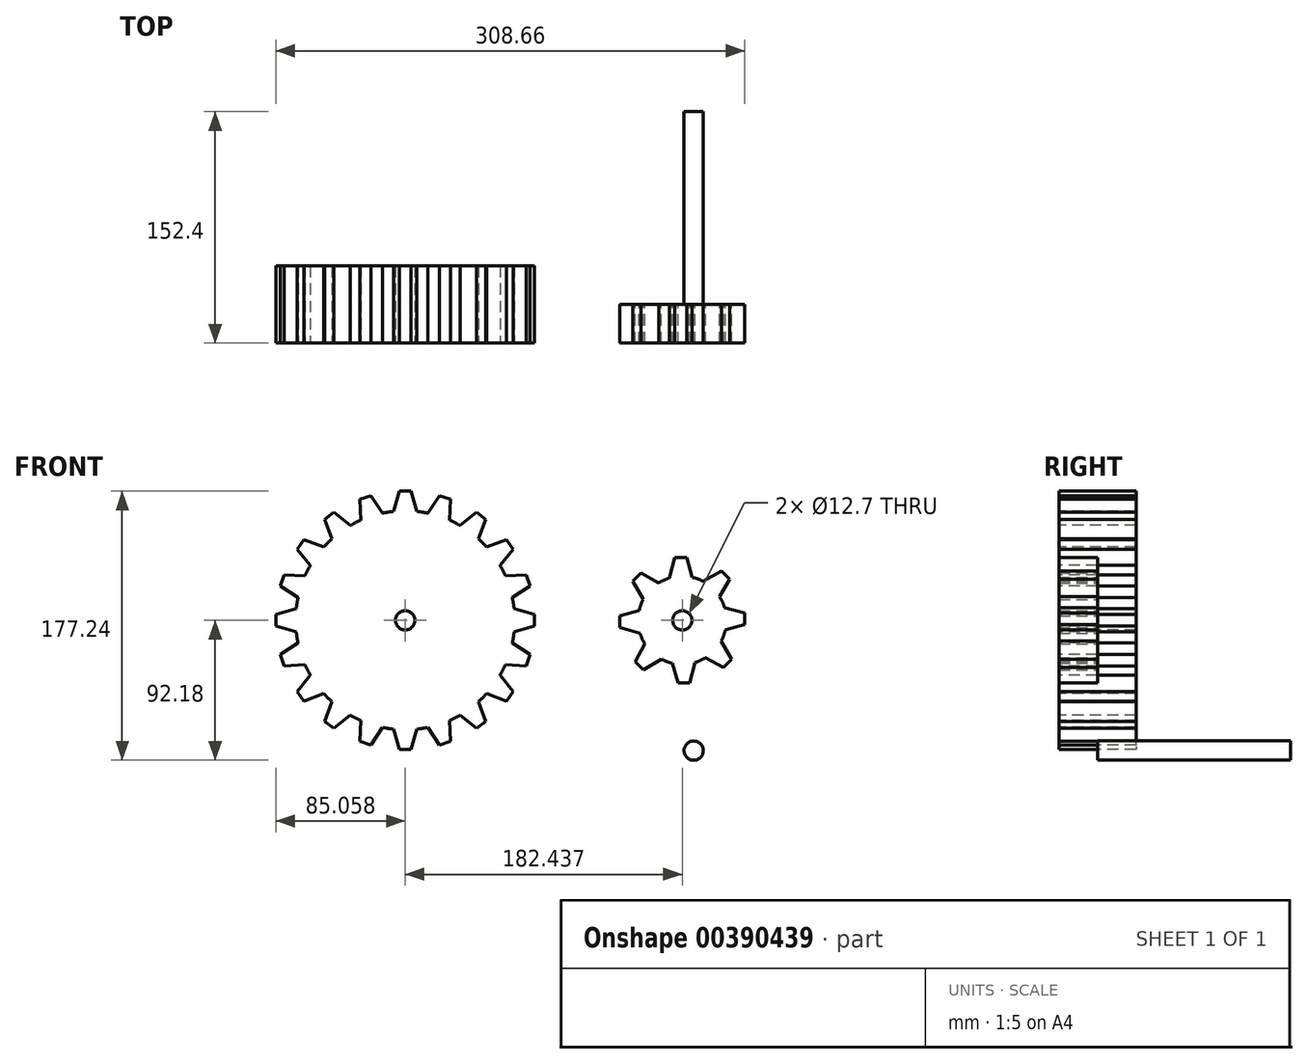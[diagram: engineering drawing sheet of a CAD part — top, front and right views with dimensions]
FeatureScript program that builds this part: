
annotation { "Feature Type Name" : "Feature", "Feature Type Description" : "" }
export const myFeature = defineFeature(function(context is Context, id is Id, definition is map)
    precondition{}
    {
        {
            var Q0;
            Q0=qCreatedBy(makeId("Front.planeOp"),FACE);
            var sketch = newSketch(context, id + "F0", { "sketchPlane" : qUnion([Q0])});
            skCircle(sketch, "E0", {"center": v(-135.26, 0) * mm, "radius": 72.11 * mm});
            skCircle(sketch, "E1", {"center": v(47.17, 0) * mm, "radius": 29.08 * mm});
            skLineSegment(sketch, "E2", {"start": v(-63.54, -7.5) * mm, "end": v(-50.2, -3.89) * mm});
            skLineSegment(sketch, "E3", {"start": v(0, 0) * mm, "end": v(-108.7, 0) * mm, "construction": true});
            skLineSegment(sketch, "E4.MirrorCS", {"start": v(-63.54, 7.5) * mm, "end": v(-50.2, 3.89) * mm});
            skLineSegment(sketch, "E5", {"start": v(-50.2, 3.89) * mm, "end": v(-50.2, -3.89) * mm});
            skLineSegment(sketch, "E6.1.0", {"start": v(-64.73, 15.02) * mm, "end": v(-53.16, 22.59) * mm});
            skLineSegment(sketch, "E6.1.1", {"start": v(-55.57, 29.98) * mm, "end": v(-53.16, 22.59) * mm});
            skLineSegment(sketch, "E6.1.2", {"start": v(-69.37, 29.3) * mm, "end": v(-55.57, 29.98) * mm});
            skLineSegment(sketch, "E6.2.0", {"start": v(-72.83, 36.08) * mm, "end": v(-64.16, 46.85) * mm});
            skLineSegment(sketch, "E6.2.1", {"start": v(-68.73, 53.14) * mm, "end": v(-64.16, 46.85) * mm});
            skLineSegment(sketch, "E6.2.2", {"start": v(-81.65, 48.23) * mm, "end": v(-68.73, 53.14) * mm});
            skLineSegment(sketch, "E6.3.0", {"start": v(-87.03, 53.61) * mm, "end": v(-82.12, 66.53) * mm});
            skLineSegment(sketch, "E6.3.1", {"start": v(-88.4, 71.1) * mm, "end": v(-82.12, 66.53) * mm});
            skLineSegment(sketch, "E6.3.2", {"start": v(-99.18, 62.44) * mm, "end": v(-88.4, 71.1) * mm});
            skLineSegment(sketch, "E6.4.0", {"start": v(-105.96, 65.9) * mm, "end": v(-105.28, 79.7) * mm});
            skLineSegment(sketch, "E6.4.1", {"start": v(-112.67, 82.1) * mm, "end": v(-105.28, 79.7) * mm});
            skLineSegment(sketch, "E6.4.2", {"start": v(-120.24, 70.53) * mm, "end": v(-112.67, 82.1) * mm});
            skLineSegment(sketch, "E6.5.0", {"start": v(-127.76, 71.72) * mm, "end": v(-131.38, 85.06) * mm});
            skLineSegment(sketch, "E6.5.1", {"start": v(-139.15, 85.06) * mm, "end": v(-131.38, 85.06) * mm});
            skLineSegment(sketch, "E6.5.2", {"start": v(-142.77, 71.72) * mm, "end": v(-139.15, 85.06) * mm});
            skLineSegment(sketch, "E6.6.0", {"start": v(-150.29, 70.53) * mm, "end": v(-157.85, 82.1) * mm});
            skLineSegment(sketch, "E6.6.1", {"start": v(-165.24, 79.7) * mm, "end": v(-157.85, 82.1) * mm});
            skLineSegment(sketch, "E6.6.2", {"start": v(-164.56, 65.9) * mm, "end": v(-165.24, 79.7) * mm});
            skLineSegment(sketch, "E6.7.0", {"start": v(-171.35, 62.44) * mm, "end": v(-182.12, 71.1) * mm});
            skLineSegment(sketch, "E6.7.1", {"start": v(-188.4, 66.53) * mm, "end": v(-182.12, 71.1) * mm});
            skLineSegment(sketch, "E6.7.2", {"start": v(-183.5, 53.61) * mm, "end": v(-188.4, 66.53) * mm});
            skLineSegment(sketch, "E6.8.0", {"start": v(-188.87, 48.23) * mm, "end": v(-201.8, 53.14) * mm});
            skLineSegment(sketch, "E6.8.1", {"start": v(-206.36, 46.85) * mm, "end": v(-201.8, 53.14) * mm});
            skLineSegment(sketch, "E6.8.2", {"start": v(-197.7, 36.08) * mm, "end": v(-206.36, 46.85) * mm});
            skLineSegment(sketch, "E6.9.0", {"start": v(-201.15, 29.3) * mm, "end": v(-214.96, 29.98) * mm});
            skLineSegment(sketch, "E6.9.1", {"start": v(-217.36, 22.59) * mm, "end": v(-214.96, 29.98) * mm});
            skLineSegment(sketch, "E6.9.2", {"start": v(-205.8, 15.02) * mm, "end": v(-217.36, 22.59) * mm});
            skLineSegment(sketch, "E6.10.0", {"start": v(-206.98, 7.5) * mm, "end": v(-220.32, 3.89) * mm});
            skLineSegment(sketch, "E6.10.1", {"start": v(-220.32, -3.89) * mm, "end": v(-220.32, 3.89) * mm});
            skLineSegment(sketch, "E6.10.2", {"start": v(-206.98, -7.5) * mm, "end": v(-220.32, -3.89) * mm});
            skLineSegment(sketch, "E6.11.0", {"start": v(-205.8, -15.02) * mm, "end": v(-217.36, -22.59) * mm});
            skLineSegment(sketch, "E6.11.1", {"start": v(-214.96, -29.98) * mm, "end": v(-217.36, -22.59) * mm});
            skLineSegment(sketch, "E6.11.2", {"start": v(-201.15, -29.3) * mm, "end": v(-214.96, -29.98) * mm});
            skLineSegment(sketch, "E6.12.0", {"start": v(-197.7, -36.08) * mm, "end": v(-206.36, -46.85) * mm});
            skLineSegment(sketch, "E6.12.1", {"start": v(-201.8, -53.14) * mm, "end": v(-206.36, -46.85) * mm});
            skLineSegment(sketch, "E6.12.2", {"start": v(-188.87, -48.23) * mm, "end": v(-201.8, -53.14) * mm});
            skLineSegment(sketch, "E6.13.0", {"start": v(-183.5, -53.61) * mm, "end": v(-188.4, -66.53) * mm});
            skLineSegment(sketch, "E6.13.1", {"start": v(-182.12, -71.1) * mm, "end": v(-188.4, -66.53) * mm});
            skLineSegment(sketch, "E6.13.2", {"start": v(-171.35, -62.44) * mm, "end": v(-182.12, -71.1) * mm});
            skLineSegment(sketch, "E6.14.0", {"start": v(-164.56, -65.9) * mm, "end": v(-165.24, -79.7) * mm});
            skLineSegment(sketch, "E6.14.1", {"start": v(-157.85, -82.1) * mm, "end": v(-165.24, -79.7) * mm});
            skLineSegment(sketch, "E6.14.2", {"start": v(-150.29, -70.53) * mm, "end": v(-157.85, -82.1) * mm});
            skLineSegment(sketch, "E6.15.0", {"start": v(-142.77, -71.72) * mm, "end": v(-139.15, -85.06) * mm});
            skLineSegment(sketch, "E6.15.1", {"start": v(-131.38, -85.06) * mm, "end": v(-139.15, -85.06) * mm});
            skLineSegment(sketch, "E6.15.2", {"start": v(-127.76, -71.72) * mm, "end": v(-131.38, -85.06) * mm});
            skLineSegment(sketch, "E6.16.0", {"start": v(-120.24, -70.53) * mm, "end": v(-112.67, -82.1) * mm});
            skLineSegment(sketch, "E6.16.1", {"start": v(-105.28, -79.7) * mm, "end": v(-112.67, -82.1) * mm});
            skLineSegment(sketch, "E6.16.2", {"start": v(-105.96, -65.9) * mm, "end": v(-105.28, -79.7) * mm});
            skLineSegment(sketch, "E6.17.0", {"start": v(-99.18, -62.44) * mm, "end": v(-88.4, -71.1) * mm});
            skLineSegment(sketch, "E6.17.1", {"start": v(-82.12, -66.53) * mm, "end": v(-88.4, -71.1) * mm});
            skLineSegment(sketch, "E6.17.2", {"start": v(-87.03, -53.61) * mm, "end": v(-82.12, -66.53) * mm});
            skLineSegment(sketch, "E6.18.0", {"start": v(-81.65, -48.23) * mm, "end": v(-68.73, -53.14) * mm});
            skLineSegment(sketch, "E6.18.1", {"start": v(-64.16, -46.85) * mm, "end": v(-68.73, -53.14) * mm});
            skLineSegment(sketch, "E6.18.2", {"start": v(-72.83, -36.08) * mm, "end": v(-64.16, -46.85) * mm});
            skLineSegment(sketch, "E6.19.0", {"start": v(-69.37, -29.3) * mm, "end": v(-55.57, -29.98) * mm});
            skLineSegment(sketch, "E6.19.1", {"start": v(-53.16, -22.59) * mm, "end": v(-55.57, -29.98) * mm});
            skLineSegment(sketch, "E6.19.2", {"start": v(-64.73, -15.02) * mm, "end": v(-53.16, -22.59) * mm});
            skLineSegment(sketch, "E7", {"start": v(75.53, -6.43) * mm, "end": v(88.34, -2.82) * mm});
            skLineSegment(sketch, "E8.MirrorCS", {"start": v(75, 8.43) * mm, "end": v(88.34, 4.8) * mm});
            skLineSegment(sketch, "E9", {"start": v(88.34, 4.8) * mm, "end": v(88.34, -2.82) * mm});
            skLineSegment(sketch, "E10.1.0", {"start": v(60.9, 25.64) * mm, "end": v(72.89, 32.5) * mm});
            skLineSegment(sketch, "E10.1.1", {"start": v(72.89, 32.5) * mm, "end": v(78.28, 27.11) * mm});
            skLineSegment(sketch, "E10.1.2", {"start": v(71.77, 15.5) * mm, "end": v(78.28, 27.11) * mm});
            skLineSegment(sketch, "E10.2.0", {"start": v(38.75, 27.83) * mm, "end": v(42.37, 41.17) * mm});
            skLineSegment(sketch, "E10.2.1", {"start": v(42.37, 41.17) * mm, "end": v(50, 41.17) * mm});
            skLineSegment(sketch, "E10.2.2", {"start": v(53.6, 28.36) * mm, "end": v(50, 41.17) * mm});
            skLineSegment(sketch, "E10.3.0", {"start": v(21.54, 13.72) * mm, "end": v(14.67, 25.71) * mm});
            skLineSegment(sketch, "E10.3.1", {"start": v(14.67, 25.71) * mm, "end": v(20.06, 31.1) * mm});
            skLineSegment(sketch, "E10.3.2", {"start": v(31.67, 24.6) * mm, "end": v(20.06, 31.1) * mm});
            skLineSegment(sketch, "E10.4.0", {"start": v(19.35, -8.43) * mm, "end": v(6, -4.8) * mm});
            skLineSegment(sketch, "E10.4.1", {"start": v(6, -4.8) * mm, "end": v(6, 2.82) * mm});
            skLineSegment(sketch, "E10.4.2", {"start": v(18.82, 6.43) * mm, "end": v(6, 2.82) * mm});
            skLineSegment(sketch, "E10.5.0", {"start": v(33.46, -25.64) * mm, "end": v(21.46, -32.5) * mm});
            skLineSegment(sketch, "E10.5.1", {"start": v(21.46, -32.5) * mm, "end": v(16.07, -27.11) * mm});
            skLineSegment(sketch, "E10.5.2", {"start": v(22.58, -15.5) * mm, "end": v(16.07, -27.11) * mm});
            skLineSegment(sketch, "E10.6.0", {"start": v(55.6, -27.83) * mm, "end": v(51.98, -41.17) * mm});
            skLineSegment(sketch, "E10.6.1", {"start": v(51.98, -41.17) * mm, "end": v(44.35, -41.17) * mm});
            skLineSegment(sketch, "E10.6.2", {"start": v(40.75, -28.36) * mm, "end": v(44.35, -41.17) * mm});
            skLineSegment(sketch, "E10.7.0", {"start": v(72.81, -13.72) * mm, "end": v(79.68, -25.71) * mm});
            skLineSegment(sketch, "E10.7.1", {"start": v(79.68, -25.71) * mm, "end": v(74.29, -31.1) * mm});
            skLineSegment(sketch, "E10.7.2", {"start": v(62.68, -24.6) * mm, "end": v(74.29, -31.1) * mm});
            skCircle(sketch, "E11", {"center": v(-135.26, 0) * mm, "radius": 6.35 * mm});
            skCircle(sketch, "E12", {"center": v(47.17, 0) * mm, "radius": 6.35 * mm});
            skCircle(sketch, "E13", {"center": v(36.26, -79.8) * mm, "radius": 6.35 * mm});
            skSolve(sketch);
        }
        {
            var Q0;
            {var subQ0=sQuery(id+"F0.wireOp",EDGE,"E6.9.0");Q0=makeQuery(id+"F0.imprint","IMPRINT",FACE,{"disambiguationData":[TD([[makeQuery(id+"F0.imprint","IMPRINT",EDGE,{"derivedFrom":subQ0}),1.0]])]});}
            var Q1;
            {var subQ0=sQuery(id+"F0.wireOp",EDGE,"E0");var subQ18=makeQuery(id+"F0.imprint","INTERSECT",VERTEX,{"derivedFrom":[subQ0,sQuery(id+"F0.wireOp",EDGE,"E4.MirrorCS")]});Q1=makeQuery(id+"F0.imprint","IMPRINT",FACE,{"disambiguationData":[TD([[makeQuery(id+"F0.imprint","IMPRINT",EDGE,{"disambiguationData":[TD([[subQ18,-1.0]])],"derivedFrom":subQ0}),1.0]])]});}
            var Q2;
            {var subQ0=sQuery(id+"F0.wireOp",EDGE,"E6.8.0");Q2=makeQuery(id+"F0.imprint","IMPRINT",FACE,{"disambiguationData":[TD([[makeQuery(id+"F0.imprint","IMPRINT",EDGE,{"derivedFrom":subQ0}),1.0]])]});}
            var Q3;
            {var subQ0=sQuery(id+"F0.wireOp",EDGE,"E6.7.0");Q3=makeQuery(id+"F0.imprint","IMPRINT",FACE,{"disambiguationData":[TD([[makeQuery(id+"F0.imprint","IMPRINT",EDGE,{"derivedFrom":subQ0}),1.0]])]});}
            var Q4;
            {var subQ0=sQuery(id+"F0.wireOp",EDGE,"E6.6.0");Q4=makeQuery(id+"F0.imprint","IMPRINT",FACE,{"disambiguationData":[TD([[makeQuery(id+"F0.imprint","IMPRINT",EDGE,{"derivedFrom":subQ0}),1.0]])]});}
            var Q5;
            {var subQ0=sQuery(id+"F0.wireOp",EDGE,"E6.5.0");Q5=makeQuery(id+"F0.imprint","IMPRINT",FACE,{"disambiguationData":[TD([[makeQuery(id+"F0.imprint","IMPRINT",EDGE,{"derivedFrom":subQ0}),1.0]])]});}
            var Q6;
            {var subQ0=sQuery(id+"F0.wireOp",EDGE,"E6.4.0");Q6=makeQuery(id+"F0.imprint","IMPRINT",FACE,{"disambiguationData":[TD([[makeQuery(id+"F0.imprint","IMPRINT",EDGE,{"derivedFrom":subQ0}),1.0]])]});}
            var Q7;
            {var subQ0=sQuery(id+"F0.wireOp",EDGE,"E6.3.0");Q7=makeQuery(id+"F0.imprint","IMPRINT",FACE,{"disambiguationData":[TD([[makeQuery(id+"F0.imprint","IMPRINT",EDGE,{"derivedFrom":subQ0}),1.0]])]});}
            var Q8;
            {var subQ0=sQuery(id+"F0.wireOp",EDGE,"E6.2.0");Q8=makeQuery(id+"F0.imprint","IMPRINT",FACE,{"disambiguationData":[TD([[makeQuery(id+"F0.imprint","IMPRINT",EDGE,{"derivedFrom":subQ0}),1.0]])]});}
            var Q9;
            {var subQ0=sQuery(id+"F0.wireOp",EDGE,"E6.1.0");Q9=makeQuery(id+"F0.imprint","IMPRINT",FACE,{"disambiguationData":[TD([[makeQuery(id+"F0.imprint","IMPRINT",EDGE,{"derivedFrom":subQ0}),1.0]])]});}
            var Q10;
            {var subQ0=sQuery(id+"F0.wireOp",EDGE,"E2");Q10=makeQuery(id+"F0.imprint","IMPRINT",FACE,{"disambiguationData":[TD([[makeQuery(id+"F0.imprint","IMPRINT",EDGE,{"derivedFrom":subQ0}),1.0]])]});}
            var Q11;
            {var subQ0=sQuery(id+"F0.wireOp",EDGE,"E6.19.0");Q11=makeQuery(id+"F0.imprint","IMPRINT",FACE,{"disambiguationData":[TD([[makeQuery(id+"F0.imprint","IMPRINT",EDGE,{"derivedFrom":subQ0}),1.0]])]});}
            var Q12;
            {var subQ0=sQuery(id+"F0.wireOp",EDGE,"E6.18.0");Q12=makeQuery(id+"F0.imprint","IMPRINT",FACE,{"disambiguationData":[TD([[makeQuery(id+"F0.imprint","IMPRINT",EDGE,{"derivedFrom":subQ0}),1.0]])]});}
            var Q13;
            {var subQ0=sQuery(id+"F0.wireOp",EDGE,"E6.17.0");Q13=makeQuery(id+"F0.imprint","IMPRINT",FACE,{"disambiguationData":[TD([[makeQuery(id+"F0.imprint","IMPRINT",EDGE,{"derivedFrom":subQ0}),1.0]])]});}
            var Q14;
            {var subQ0=sQuery(id+"F0.wireOp",EDGE,"E6.16.0");Q14=makeQuery(id+"F0.imprint","IMPRINT",FACE,{"disambiguationData":[TD([[makeQuery(id+"F0.imprint","IMPRINT",EDGE,{"derivedFrom":subQ0}),1.0]])]});}
            var Q15;
            {var subQ0=sQuery(id+"F0.wireOp",EDGE,"E6.15.0");Q15=makeQuery(id+"F0.imprint","IMPRINT",FACE,{"disambiguationData":[TD([[makeQuery(id+"F0.imprint","IMPRINT",EDGE,{"derivedFrom":subQ0}),1.0]])]});}
            var Q16;
            {var subQ0=sQuery(id+"F0.wireOp",EDGE,"E6.14.0");Q16=makeQuery(id+"F0.imprint","IMPRINT",FACE,{"disambiguationData":[TD([[makeQuery(id+"F0.imprint","IMPRINT",EDGE,{"derivedFrom":subQ0}),1.0]])]});}
            var Q17;
            {var subQ0=sQuery(id+"F0.wireOp",EDGE,"E6.13.0");Q17=makeQuery(id+"F0.imprint","IMPRINT",FACE,{"disambiguationData":[TD([[makeQuery(id+"F0.imprint","IMPRINT",EDGE,{"derivedFrom":subQ0}),1.0]])]});}
            var Q18;
            {var subQ0=sQuery(id+"F0.wireOp",EDGE,"E6.12.0");Q18=makeQuery(id+"F0.imprint","IMPRINT",FACE,{"disambiguationData":[TD([[makeQuery(id+"F0.imprint","IMPRINT",EDGE,{"derivedFrom":subQ0}),1.0]])]});}
            var Q19;
            {var subQ0=sQuery(id+"F0.wireOp",EDGE,"E6.11.0");Q19=makeQuery(id+"F0.imprint","IMPRINT",FACE,{"disambiguationData":[TD([[makeQuery(id+"F0.imprint","IMPRINT",EDGE,{"derivedFrom":subQ0}),1.0]])]});}
            var Q20;
            {var subQ0=sQuery(id+"F0.wireOp",EDGE,"E6.10.0");Q20=makeQuery(id+"F0.imprint","IMPRINT",FACE,{"disambiguationData":[TD([[makeQuery(id+"F0.imprint","IMPRINT",EDGE,{"derivedFrom":subQ0}),1.0]])]});}
            extrude(context, id + "F1", {"entities" : qUnion([Q0, Q1, Q2, Q3, Q4, Q5, Q6, Q7, Q8, Q9, Q10, Q11, Q12, Q13, Q14, Q15, Q16, Q17, Q18, Q19, Q20]), "oppositeDirection" : true, "depth" : 25.4 * mm});
        }
        {
            var Q0;
            Q0 = qSketchRegion(id + "F0", true);
            extrude(context, id + "F2", {"entities" : qUnion([Q0]), "operationType" : NewBodyOperationType.ADD, "depth" : 25.4 * mm});
        }
        {
            var Q0;
            Q0=makeQuery(id+"F2.opExtrude","SWEPT_BODY",BODY,{"disambiguationData":[OSD([sQuery(id+"F0.wireOp",EDGE,"E13")])]});
            deleteBodies(context, id + "F3", {"entities" : qUnion([Q0])});
        }
        {
            var Q0;
            Q0=qCreatedBy(makeId("Front.planeOp"),FACE);
            var sketch = newSketch(context, id + "F4", { "sketchPlane" : qUnion([Q0])});
            skCircle(sketch, "E14", {"center": v(54.7, -85.83) * mm, "radius": 6.35 * mm});
            skSolve(sketch);
        }
        {
            var Q0;
            Q0=makeQuery(id+"F4.imprint","IMPRINT",FACE,{"disambiguationData":[TD([[makeQuery(id+"F4.imprint","IMPRINT",EDGE,{"derivedFrom":sQuery(id+"F4.wireOp",EDGE,"E14")}),1.0]])]});
            extrude(context, id + "F5", {"entities" : qUnion([Q0]), "oppositeDirection" : true, "depth" : 127 * mm});
        }
    });
